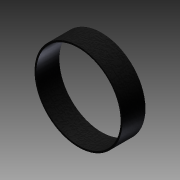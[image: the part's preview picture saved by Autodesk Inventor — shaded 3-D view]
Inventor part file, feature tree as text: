
AUTODESK INVENTOR PART (.ipt)
format: ipt  version: 2012 (Build 160160000, 160)  size: 79,360 bytes
history: native  units: in
note: dims shown in document units (in); Inventor stores cm internally (conversion verified against a paired STEP export)
features: extrude x1, sketch x1
ambient origin geometry x8: Origin, YZ Plane, XZ Plane, XY Plane, X Axis, Y Axis, Z Axis, Center Point
bodies: Solid1 (feature_tree)
feature tree (2):
  extrude  "Extrusion1"  Depth=1.375in
  sketch  "Sketch1"  dims[d0=1.431in d1=1.375in d2=0.375in d3=0.0in]
